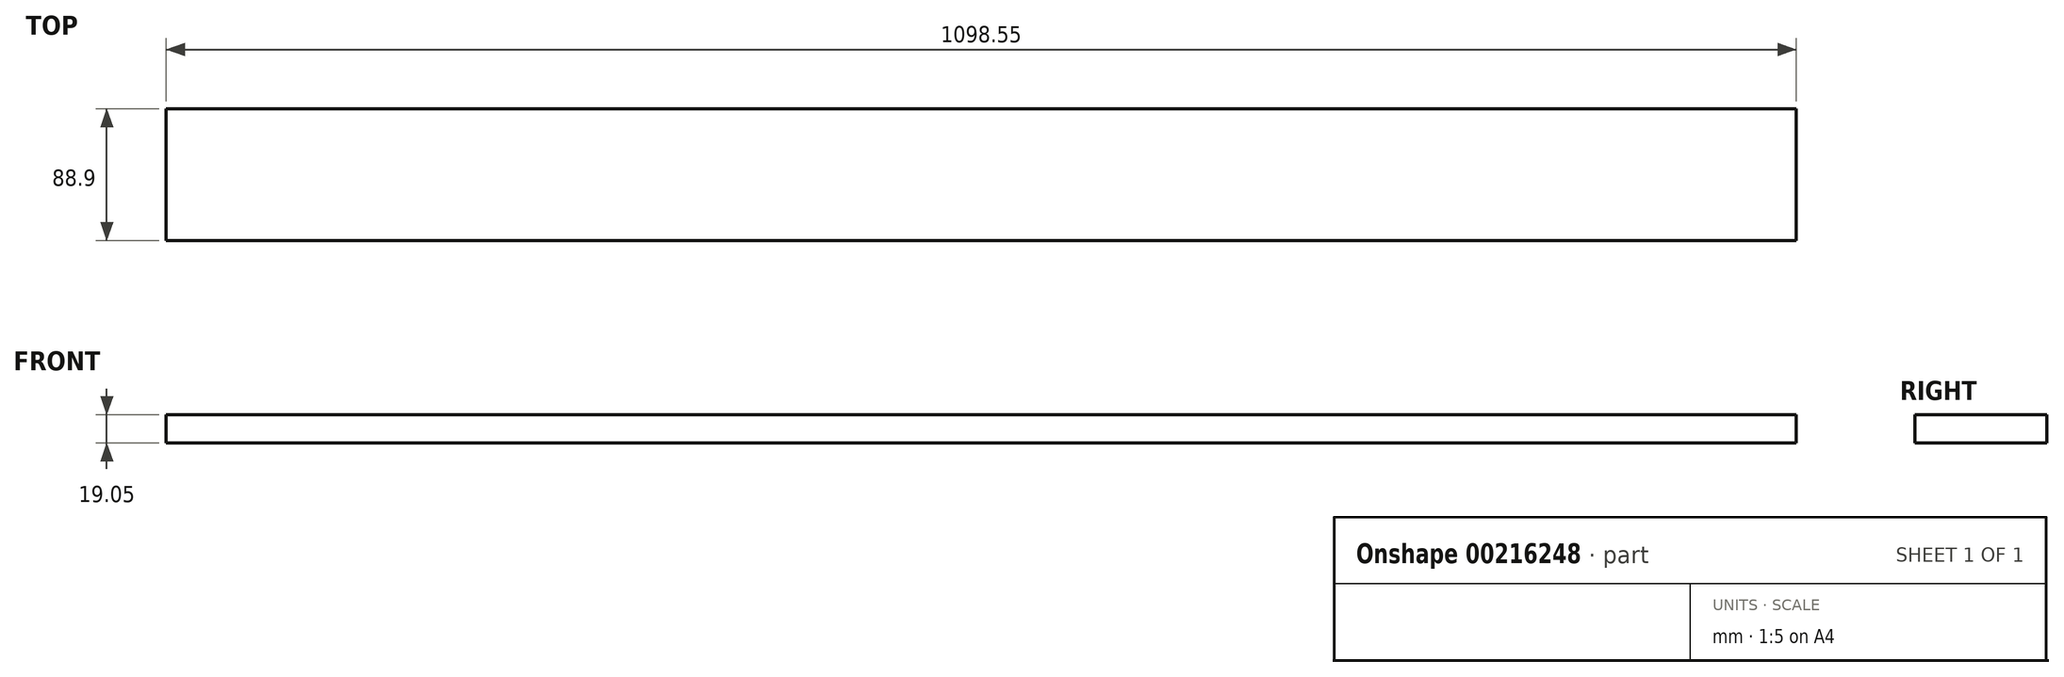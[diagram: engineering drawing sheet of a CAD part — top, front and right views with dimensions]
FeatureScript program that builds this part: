
annotation { "Feature Type Name" : "Feature", "Feature Type Description" : "" }
export const myFeature = defineFeature(function(context is Context, id is Id, definition is map)
    precondition{}
    {
        {
            var Q0;
            Q0=qCreatedBy(makeId("Top.planeOp"),FACE);
            var sketch = newSketch(context, id + "F0", { "sketchPlane" : qUnion([Q0])});
            skLineSegment(sketch, "E0", {"start": v(-3525.79, 341.69) * mm, "end": v(-2427.24, 341.69) * mm});
            skLineSegment(sketch, "E1", {"start": v(-2427.24, 341.69) * mm, "end": v(-2427.24, 430.59) * mm});
            skLineSegment(sketch, "E2", {"start": v(-2427.24, 430.59) * mm, "end": v(-3525.79, 430.59) * mm});
            skLineSegment(sketch, "E3", {"start": v(-3525.79, 430.59) * mm, "end": v(-3525.79, 341.69) * mm});
            skSolve(sketch);
        }
        {
            var Q0;
            Q0=makeQuery(id+"F0.imprint","IMPRINT",FACE,{"disambiguationData":[TD([[makeQuery(id+"F0.imprint","IMPRINT",EDGE,{"derivedFrom":sQuery(id+"F0.wireOp",EDGE,"E0")}),1.0]])]});
            extrude(context, id + "F1", {"entities" : qUnion([Q0]), "depth" : 19.05 * mm});
        }
    });
